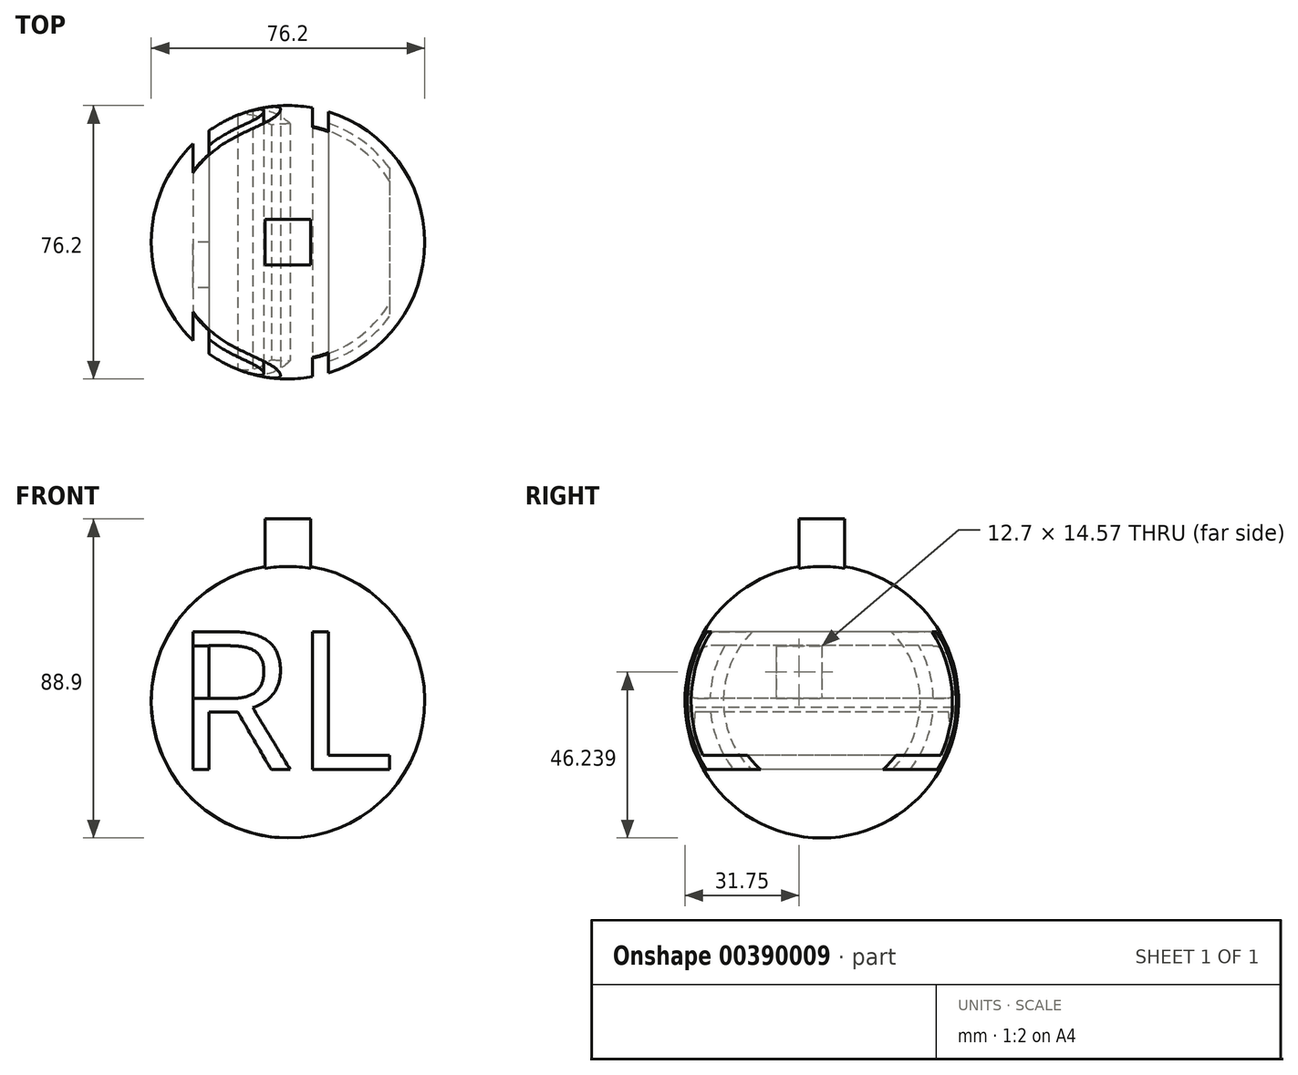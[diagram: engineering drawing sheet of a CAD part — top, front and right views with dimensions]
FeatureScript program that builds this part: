
annotation { "Feature Type Name" : "Feature", "Feature Type Description" : "" }
export const myFeature = defineFeature(function(context is Context, id is Id, definition is map)
    precondition{}
    {
        {
            var Q0;
            Q0=qCreatedBy(makeId("Front.planeOp"),FACE);
            var sketch = newSketch(context, id + "F0", { "sketchPlane" : qUnion([Q0])});
            skLineSegment(sketch, "E0", {"start": v(0, 0) * mm, "end": v(0, 76.2) * mm});
            skArc(sketch, "E1", {"start": v(0, 0) * mm, "mid": v(38.1, 38.1) * mm, "end": v(0, 76.2) * mm});
            skSolve(sketch);
        }
        {
            var Q0;
            Q0=makeQuery(id+"F0.imprint","IMPRINT",FACE,{"disambiguationData":[TD([[makeQuery(id+"F0.imprint","IMPRINT",EDGE,{"derivedFrom":sQuery(id+"F0.wireOp",EDGE,"E0")}),-1.0]])]});
            var Q1;
            Q1=sQuery(id+"F0.wireOp",EDGE,"E0");
            revolve(context, id + "F1", {"entities" : qUnion([Q0]), "axis" : qUnion([Q1]), "revolveType" : RevolveType.FULL});
        }
        {
            var Q0;
            Q0=qCreatedBy(makeId("Top.planeOp"),FACE);
            cPlane(context, id + "F2", {"entities" : qUnion([Q0]), "cplaneType" : CPlaneType.OFFSET, "offset" : 88.9 * mm, "width" : 152.4 * mm, "height" : 152.4 * mm});
        }
        {
            var Q0;
            Q0=qCreatedBy(id+"F2.planeOp",FACE);
            var sketch = newSketch(context, id + "F3", { "sketchPlane" : qUnion([Q0])});
            skLineSegment(sketch, "E2.bottom", {"start": v(-6.35, 6.35) * mm, "end": v(6.35, 6.35) * mm});
            skLineSegment(sketch, "E2.top", {"start": v(-6.35, -6.35) * mm, "end": v(6.35, -6.35) * mm});
            skLineSegment(sketch, "E2.left", {"start": v(-6.35, 6.35) * mm, "end": v(-6.35, -6.35) * mm});
            skLineSegment(sketch, "E2.right", {"start": v(6.35, 6.35) * mm, "end": v(6.35, -6.35) * mm});
            skPoint(sketch, "E2.middle", {"position": v(0, 0) * mm});
            skSolve(sketch);
        }
        {
            var Q0;
            Q0=makeQuery(id+"F3.imprint","IMPRINT",FACE,{"disambiguationData":[TD([[makeQuery(id+"F3.imprint","IMPRINT",EDGE,{"derivedFrom":sQuery(id+"F3.wireOp",EDGE,"E2.bottom")}),-1.0]])]});
            extrude(context, id + "F4", {"entities" : qUnion([Q0]), "operationType" : NewBodyOperationType.ADD, "oppositeDirection" : true, "depth" : 25.4 * mm});
        }
        {
            var Q0;
            Q0=qCreatedBy(makeId("Front.planeOp"),FACE);
            var sketch = newSketch(context, id + "F5", { "sketchPlane" : qUnion([Q0])});
            skText(sketch, "E3", { "text": "RL", "fontName": "OpenSans-Regular.ttf"});
            skPoint(sketch, "E4.bottom.start.orphan", {"position": v(-21.44, 39.03) * mm});
            skPoint(sketch, "E4.right.end.orphan", {"position": v(-29.8, 53.47) * mm});
            skPoint(sketch, "E4.right.start.orphan", {"position": v(-29.8, 39.03) * mm});
            const initialGuessF5  = {"E3": [-0.03175, 0.01905, 1, 0, 0.03878]};
            skSetInitialGuess(sketch, initialGuessF5);
            skSolve(sketch);
        }
        {
            var Q0;
            Q0 = qSketchRegion(id + "F5", true);
            extrude(context, id + "F6", {"entities" : qUnion([Q0]), "operationType" : NewBodyOperationType.REMOVE, "endBound" : BoundingType.SYMMETRIC, "oppositeDirection" : true, "depth" : 203.2 * mm});
        }
        {
            var Q0;
            Q0=qCreatedBy(makeId("Front.planeOp"),FACE);
            var sketch = newSketch(context, id + "F7", { "sketchPlane" : qUnion([Q0])});
            skLineSegment(sketch, "E5.bottom", {"start": v(-21.47, 38.95) * mm, "end": v(-28.7, 38.95) * mm});
            skLineSegment(sketch, "E5.top", {"start": v(-21.47, 53.52) * mm, "end": v(-28.7, 53.52) * mm});
            skLineSegment(sketch, "E5.left", {"start": v(-21.47, 38.95) * mm, "end": v(-21.47, 53.52) * mm});
            skLineSegment(sketch, "E5.right", {"start": v(-28.7, 38.95) * mm, "end": v(-28.7, 53.52) * mm});
            skSolve(sketch);
        }
        {
            var Q0;
            Q0=makeQuery(id+"F7.imprint","IMPRINT",FACE,{"disambiguationData":[TD([[makeQuery(id+"F7.imprint","IMPRINT",EDGE,{"derivedFrom":sQuery(id+"F7.wireOp",EDGE,"E5.bottom")}),-1.0]])]});
            extrude(context, id + "F8", {"entities" : qUnion([Q0]), "operationType" : NewBodyOperationType.ADD, "depth" : 12.7 * mm});
        }
    });
